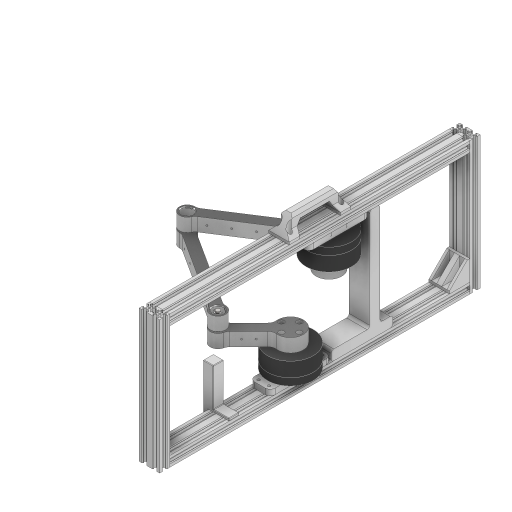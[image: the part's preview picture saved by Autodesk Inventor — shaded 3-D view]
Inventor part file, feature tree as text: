
AUTODESK INVENTOR PART (.ipt)
format: ipt  version: 2024.2 (Build 282272000, 272)  size: 2,525,696 bytes
history: native  units: mm
features: extrude x55, sketch x40, projected_geometry x22, other x20, plane x12, chamfer x7, mirror x5, pattern_circular x4, fillet x4, split x1, revolve x1
ambient origin geometry x8: Origin, YZ Plane, XZ Plane, XY Plane, X Axis, Y Axis, Z Axis, Center Point
bodies: Solid14 (feature_tree), Solid35 (feature_tree), Solid37 (feature_tree), Solid38 (feature_tree), Solid40 (feature_tree), Solid45 (feature_tree)
feature tree (171):
  other  "Proximal Link 1"
  sketch  "Sketch1"  dims[d42=1000.0mm d43=1000.0mm]
  extrude  "Extrusion6"  Depth=1000.0mm
  extrude  "Extrusion7"  Depth=20.0mm
  extrude  "Extrusion13"  Depth=20.0mm
  extrude  "Extrusion8"  Depth=20.0mm
  extrude  "Extrusion10"  Depth=100.0mm
  extrude  "Extrusion9"  Depth=200.0mm
  extrude  "Extrusion11"  Depth=26.0mm
  sketch  "Sketch6"  dims[d45=75.0mm d46=20.0mm]
  extrude  "Extrusion19"  Depth=58.0mm
  extrude  "Extrusion21"  Depth=87.0mm
  extrude  "Extrusion22"  Depth=32.0mm
  extrude  "Extrusion34"  Depth=61.0mm
  plane  "Work Plane9"
  sketch  "Sketch11"  dims[d47=20.0mm d48=20.0mm]
  other  "Work Axis2"
  sketch  "Sketch12"  dims[d49=20.0mm d50=20.0mm]
  extrude  "Extrusion23"  Depth=21.424855mm
  extrude  "Extrusion38"  Depth=154.809503mm
  extrude  "Extrusion39"  Depth=54.105339mm
  plane  "Work Plane10"
  split  "Split1"
  pattern_circular  "Circular Pattern3"  Count=100  [1 undecoded]
  extrude  "Extrusion37"  Depth=35.0mm
  fillet  "Fillet1"  Radius=16.0mm
  plane  "Work Plane21"
  extrude  "Extrusion40"  Depth=7.0mm TaperAngle=0.0deg
  extrude  "Extrusion41"  Depth=89.0mm
  pattern_circular  "Circular Pattern4"  Count=2 Angle=360.0deg
  plane  "Work Plane13"
  extrude  "Extrusion42"  TaperAngle=45.0deg  [1 undecoded]
  mirror  "Mirror6"
  sketch  "Sketch21"  dims[d64=0.0mm d65=32.0mm]
  extrude  "Extrusion43"  Depth=50.0mm
  sketch  "Sketch22"  dims[d66=0.0mm d67=61.0mm]
  extrude  "Extrusion44"  [1 undecoded]
  sketch  "Sketch23"  dims[d68=0.0mm d71=21.424855mm]
  extrude  "Extrusion45"  Depth=8.0mm
  plane  "Work Plane14"
  sketch  "Sketch25"  dims[d74=54.105339mm d75=35.355339mm]
  extrude  "Extrusion51"  TaperAngle=0.0deg  [1 undecoded]
  extrude  "Extrusion52"  Depth=3.0mm
  fillet  "Fillet2"  [1 undecoded]
  sketch  "Sketch24"  dims[d72=9.991072mm d73=154.809503mm]
  extrude  "Extrusion53"  Depth=15.0mm
  extrude  "Extrusion54"  Depth=6.0mm TaperAngle=0.0deg
  extrude  "Extrusion58"  Depth=8.0mm
  extrude  "Extrusion59"  Depth=10.0mm
  plane  "Work Plane18"
  extrude  "Extrusion61"  Depth=20.0mm TaperAngle=360.0deg
  extrude  "Extrusion62"  Depth=0.75mm TaperAngle=0.0deg
  sketch  "Sketch37"  dims[d80=0.0mm]
  extrude  "Extrusion63"  Depth=0.75mm TaperAngle=0.0deg
  extrude  "Extrusion64"  Depth=0.75mm TaperAngle=0.0deg
  chamfer  "Chamfer2"  Distance=660.0mm
  extrude  "Extrusion66"  Depth=40.0mm
  extrude  "Extrusion65"  Depth=20.0mm
  extrude  "Extrusion67"  Depth=10.0mm
  chamfer  "Chamfer3"  Distance=5.0mm
  plane  "Work Plane19"
  mirror  "Mirror10"
  mirror  "Mirror11"
  extrude  "Extrusion68"  Depth=26.0mm TaperAngle=0.0deg
  plane  "Work Plane20"
  mirror  "Mirror12"
  sketch  "Sketch42"  dims[d105=1000.0mm d106=0.0mm d107=35.0mm d108=4.3mm d109=16.0mm]
  extrude  "Extrusion69"  Depth=6.0mm TaperAngle=0.0deg
  sketch  "Sketch43"  dims[d110=0.0mm d111=7.0mm d112=0.0mm]
  extrude  "Extrusion70"  Depth=10.0mm
  sketch  "Sketch44"  dims[d113=89.0mm d114=30.0mm]
  extrude  "Extrusion71"  Depth=20.0mm TaperAngle=0.0deg
  sketch  "Sketch45"  dims[d115=4.3mm]
  other  "Work Axis3"
  pattern_circular  "Circular Pattern6"  Count=2  [1 undecoded]
  extrude  "Extrusion78"  Depth=11.0mm TaperAngle=0.0deg
  extrude  "Extrusion79"  Depth=20.0mm TaperAngle=0.0deg
  fillet  "Fillet3"  [1 undecoded]
  plane  "Work Plane22"
  plane  "Work Plane23"
  extrude  "Extrusion80"  TaperAngle=0.0deg  [1 undecoded]
  mirror  "Mirror13"
  chamfer  "Chamfer4"  [1 undecoded]
  extrude  "Extrusion88"  Depth=20.0mm
  extrude  "Extrusion89"  Depth=40.0mm
  pattern_circular  "Circular Pattern7"  [2 undecoded]
  sketch  "Sketch52"  dims[d158=7.0mm d159=0.0mm]
  extrude  "Extrusion90"  Depth=5.0mm
  extrude  "Extrusion93"  Depth=5.0mm
  extrude  "Extrusion94"  Depth=0.75mm
  chamfer  "Chamfer6"  Distance=10.0mm
  sketch  "Sketch53"  dims[d166=2.0mm d167=3.0mm d168=0.0mm]
  extrude  "Extrusion95"  Depth=40.0mm TaperAngle=0.0deg
  plane  "Work Plane24"
  extrude  "Extrusion96"  Depth=5.0mm TaperAngle=0.0deg
  chamfer  "Chamfer7"  Distance=35.0mm Angle=45.0deg
  chamfer  "Chamfer8"  Distance=5.3mm
  extrude  "Extrusion97"  TaperAngle=0.0deg  [1 undecoded]
  extrude  "Extrusion98"  Depth=10.0mm
  sketch  "Sketch55"  dims[d171=30.0mm d172=0.0mm d173=6.0mm d174=0.0mm]
  extrude  "Extrusion99"  Depth=0.75mm
  extrude  "Extrusion100"  Depth=0.75mm
  extrude  "Extrusion101"  Depth=1.35mm TaperAngle=0.0deg
  extrude  "Extrusion102"  Depth=1.35mm TaperAngle=45.0deg
  chamfer  "Chamfer9"  Distance=10.0mm
  plane  "Work Plane25"
  revolve  "Revolution1"  [1 undecoded]
  extrude  "Extrusion103"  Depth=20.0mm
  fillet  "Fillet4"  Radius=20.0mm
  other  "Distal Link 1"
  other  "Distal Link 2"
  other  "Proximal Link 2"
  other  "Spacer"
  other  "Pattern of Solid22:2"
  other  "Motor 2 Stator"
  other  "Pattern of Solid23:3"
  other  "Motor 2 Rotor"
  sketch  "Sketch14"  dims[d51=100.0mm d52=100.0mm]
  other  "Bearing"
  sketch  "Sketch16"  dims[d53=200.0mm d54=200.0mm]
  other  "separator"
  sketch  "Sketch17"  dims[d57=26.0mm d58=0.0mm d59=29.0mm]
  other  "rod"
  sketch  "Sketch19"  dims[d60=0.0mm d61=58.0mm]
  sketch  "Sketch20"  dims[d62=0.0mm d63=87.0mm]
  projected_geometry  "Projected Loop43"
  projected_geometry  "Projected Loop44"
  sketch  "Sketch31"  dims[d76=72.855339mm]
  projected_geometry  "Projected Loop48"
  projected_geometry  "Projected Loop49"
  sketch  "Sketch32"  dims[d77=13.570873mm]
  sketch  "Sketch35"  dims[d78=37.5mm]
  sketch  "Sketch36"  dims[d79=3.0mm]
  projected_geometry  "Projected Loop53"
  projected_geometry  "Projected Loop54"
  sketch  "Sketch38"  dims[d83=35.0mm]
  projected_geometry  "Projected Loop56"
  sketch  "Sketch39"  dims[d84=4.3mm]
  sketch  "Sketch40"  dims[d87=22.1mm]
  projected_geometry  "Projected Loop57"
  projected_geometry  "Projected Loop59"
  projected_geometry  "Projected Loop60"
  projected_geometry  "Projected Loop61"
  projected_geometry  "Projected Loop62"
  sketch  "Sketch41"  dims[d96=0.15mm d101=1000.0mm d102=0.0mm]
  projected_geometry  "Projected Loop63"
  projected_geometry  "Projected Loop64"
  sketch  "Sketch46"  dims[d116=42.0mm d117=0.0mm d123=20.0mm d124=360.0deg]
  other  "aligner"
  sketch  "Sketch47"  dims[d126=45.0deg d127=45.0deg]
  projected_geometry  "Projected Loop65"
  sketch  "Sketch48"  dims[d128=30.0mm d135=50.0mm]
  sketch  "Sketch50"  dims[d142=1.0mm d155=-14.0mm]
  sketch  "Sketch51"  dims[d156=22.0mm d157=8.0mm]
  projected_geometry  "Projected Loop66"
  other  "motor zero aligner"
  other  "handle"
  sketch  "Sketch54"  dims[d169=0.15mm d170=15.0mm]
  projected_geometry  "Projected Loop67"
  projected_geometry  "Projected Loop68"
  projected_geometry  "Projected Loop69"
  projected_geometry  "Projected Loop70"
  sketch  "Sketch56"  dims[d175=8.0mm d176=55.0mm]
  sketch  "Sketch57"  dims[d177=0.0mm d231=10.0mm]
  projected_geometry  "Projected Loop71"
  sketch  "Sketch58"  dims[d232=9.0mm d233=0.0mm d234=20.0mm d235=360.0deg]
  sketch  "Sketch59"  dims[d237=0.1mm d238=0.0mm d239=3.0mm d240=0.0mm d241=3.0mm d242=0.0mm d243=3.0mm d244=0.0mm d245=660.0mm d246=40.0mm d247=20.0mm d248=10.0mm d250=5.0mm d269=26.0mm d270=0.0mm d271=6.0mm d272=0.0mm d273=10.0mm d274=20.0mm d275=0.0mm d276=20.0mm d277=0.0mm d284=11.0mm d285=0.0mm d286=20.0mm d287=0.0mm d288=-7.0mm d306=0.0mm d307=0.0mm d309=40.0mm d310=4.2mm d311=20.0mm d312=20.0mm d313=1.8mm d314=4.3mm d315=6.25mm d316=9.16mm d317=11.0mm d318=1.5mm d319=45.0deg d320=360.0deg d321=1.8mm d322=1.0mm d324=40.0mm d325=4.2mm d326=20.0mm d327=20.0mm d328=1.8mm d329=4.3mm d330=6.25mm d331=9.16mm d332=11.0mm d333=1.5mm d334=45.0deg d335=360.0deg d336=1.8mm d337=1.0mm d338=0.0mm d339=0.0mm d355=20.0mm d356=40.0mm d357=5.0mm d358=5.0mm d359=5.0mm d360=5.3mm d361=10.0mm d362=40.0mm d363=0.0mm d364=5.0mm d365=0.0mm d366=35.0mm d367=2.0mm d368=45.0deg d369=5.3mm d370=0.0mm d371=0.0mm d374=10.0mm d375=7.4mm d377=30.0mm d378=1.35mm d379=0.0mm d380=1.35mm d381=2.0mm d382=45.0deg d386=10.0mm d388=30.0mm d389=1.35mm d390=0.0mm d392=40.0mm d393=4.2mm d394=20.0mm d395=20.0mm d396=1.8mm d397=4.3mm d398=6.25mm d399=9.16mm d400=11.0mm d401=1.5mm d402=45.0deg d403=360.0deg d404=1.8mm d405=1.0mm d407=40.0mm d408=4.2mm d409=20.0mm d410=20.0mm d411=1.8mm d412=4.3mm d413=6.25mm d414=9.16mm d415=11.0mm d416=1.5mm d417=45.0deg d418=360.0deg d419=1.8mm d420=1.0mm d421=20.0mm d422=20.0mm d423=20.0mm d424=0.0mm d425=5.3mm d426=15.0mm d427=15.0mm d428=5.3mm d429=15.0mm d430=15.0mm d431=20.0mm d432=-1.5mm d433=3.0mm d434=0.0mm d435=3.0mm d436=0.0mm d437=3.0mm d438=0.0mm d439=40.0mm d447=14.0mm d449=14.0mm d453=14.0mm d456=14.0mm d459=14.0mm d462=14.0mm d465=20.0mm d466=360.0deg d468=20.0mm d469=1.0mm d470=0.0mm d471=40.0mm d472=20.0mm d473=120.0mm d474=0.0mm d475=5.0mm d476=-3.0mm d477=7.0mm d478=1.1mm d479=0.0mm d480=20.0mm d482=20.0mm d486=20.0mm d490=20.0mm d497=20.0mm d501=20.0mm d505=20.0mm d506=25.0mm d507=20.0mm d508=25.0mm d509=25.0mm d510=20.0mm d511=20.0mm d512=25.0mm d513=20.0mm d514=25.0mm d515=20.0mm d516=25.0mm d517=1.5mm d518=2.0mm d519=45.0deg d536=3.3mm d537=3.3mm d538=20.0mm d539=0.0mm d540=0.0mm d541=70.0mm d542=70.0mm d543=3.3mm d545=0.0mm d546=0.0mm d547=20.0mm d548=360.0deg d550=10.0mm d553=5.0mm d554=0.0mm d557=0.0mm d565=20.0mm d566=20.0mm d567=5.0mm d568=0.0mm d569=10.0mm d570=0.0mm d571=1.0mm d572=2.0mm d573=45.0deg d574=120.0mm d575=20.0mm d576=20.0mm d577=10.0mm d578=10.0mm d579=5.3mm d580=5.3mm d581=5.3mm d582=5.3mm d583=5.0mm d584=0.0mm d585=-10.0mm d586=60.0deg d587=60.0deg d588=20.0mm d589=20.0mm d590=0.0mm d591=10.0mm d592=2.0mm d593=45.0deg d594=5.0mm d595=2.0mm d596=45.0deg d597=9.0mm d598=0.0mm d599=0.0mm d600=5.0mm d601=0.0mm d602=5.0mm d603=5.0mm d604=3.1mm d605=2.0mm d606=0.0mm d607=2.0mm d608=0.0mm d609=0.0mm d610=0.0mm d611=4.0mm d612=0.0mm d613=2.0mm d614=2.0mm d615=45.0deg d616=1.0mm d617=40.0mm d618=90.0deg d619=0.1mm d620=0.1mm d626=7.0mm d630=13.0mm d634=11.5mm d641=7.330383mm d642=12.217305mm d643=12.217305mm d646=9.582036mm d648=4.014257mm d650=1.0mm d651=0.0mm d652=0.75mm]
  projected_geometry  "Projected Loop72"
  other  "segger"
  other  "Motor 1 Stator"
  other  "Motor 1 Rotor"
note: 13 required parameter values undecoded (feature->parameter linkage not recoverable at this tier; creation-order binding heuristic only, values carry confidence <= 0.55)